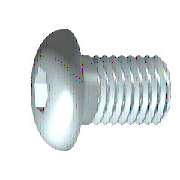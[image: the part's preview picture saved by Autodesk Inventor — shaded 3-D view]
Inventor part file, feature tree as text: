
AUTODESK INVENTOR PART (.ipt)
format: ipt  version: 2012 (Build 160160000, 160)  size: 202,240 bytes
history: native  units: mm (DEFAULTED — no unit token found)
features: extrude x1, plane x1, fillet x1
ambient origin geometry x7: Origin, YZ Plane, XY Plane, X Axis, Y Axis, Z Axis, Center Point
bodies: Solid1 (feature_tree), Body (feature_tree)
feature tree (3):
  extrude  "Slot"  Depth=7.93476mm
  plane  "Work Plane1"
  fillet  "Fillet2"  Radius=1.59014mm
